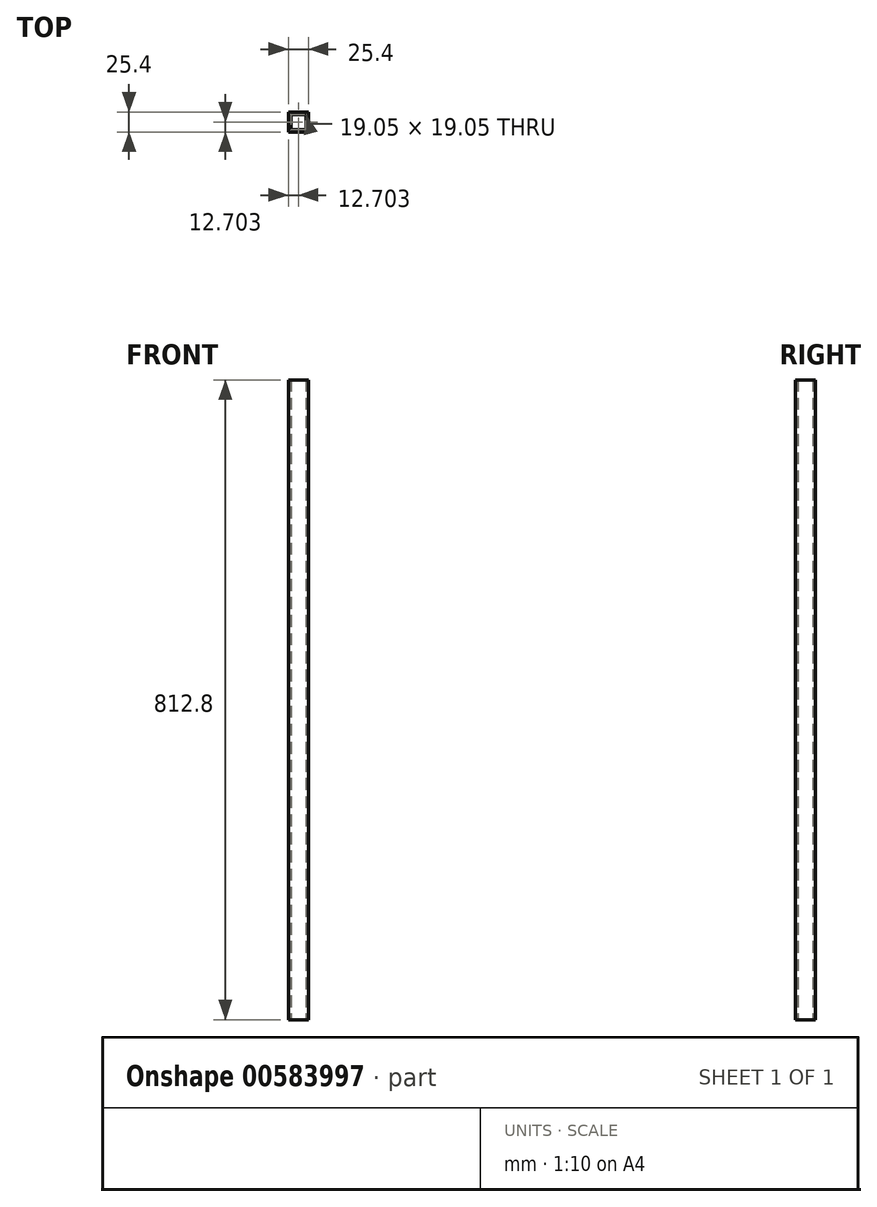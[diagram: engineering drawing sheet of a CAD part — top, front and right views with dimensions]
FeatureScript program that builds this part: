
annotation { "Feature Type Name" : "Feature", "Feature Type Description" : "" }
export const myFeature = defineFeature(function(context is Context, id is Id, definition is map)
    precondition{}
    {
        {
            var Q0;
            Q0=qCreatedBy(makeId("Top.planeOp"),FACE);
            var sketch = newSketch(context, id + "F0", { "sketchPlane" : qUnion([Q0])});
            skLineSegment(sketch, "E0.bottom", {"start": v(-6.57, 8.24) * mm, "end": v(12.48, 8.24) * mm});
            skLineSegment(sketch, "E0.top", {"start": v(-6.57, -10.81) * mm, "end": v(12.48, -10.81) * mm});
            skLineSegment(sketch, "E0.left", {"start": v(-6.57, 8.24) * mm, "end": v(-6.57, -10.81) * mm});
            skLineSegment(sketch, "E0.right", {"start": v(12.48, 8.24) * mm, "end": v(12.48, -10.81) * mm});
            skLineSegment(sketch, "E1.bottom", {"start": v(-9.75, 11.41) * mm, "end": v(15.65, 11.41) * mm});
            skLineSegment(sketch, "E1.top", {"start": v(-9.75, -13.99) * mm, "end": v(15.65, -13.99) * mm});
            skLineSegment(sketch, "E1.left", {"start": v(-9.75, 11.41) * mm, "end": v(-9.75, -13.99) * mm});
            skLineSegment(sketch, "E1.right", {"start": v(15.65, 11.41) * mm, "end": v(15.65, -13.99) * mm});
            skSolve(sketch);
        }
        {
            var Q0;
            Q0=makeQuery(id+"F0.imprint","IMPRINT",FACE,{"disambiguationData":[TD([[makeQuery(id+"F0.imprint","IMPRINT",EDGE,{"derivedFrom":sQuery(id+"F0.wireOp",EDGE,"E0.bottom")}),1.0]])]});
            extrude(context, id + "F1", {"entities" : qUnion([Q0]), "depth" : 812.8 * mm, "offsetDistance" : 25.4 * mm});
        }
    });
